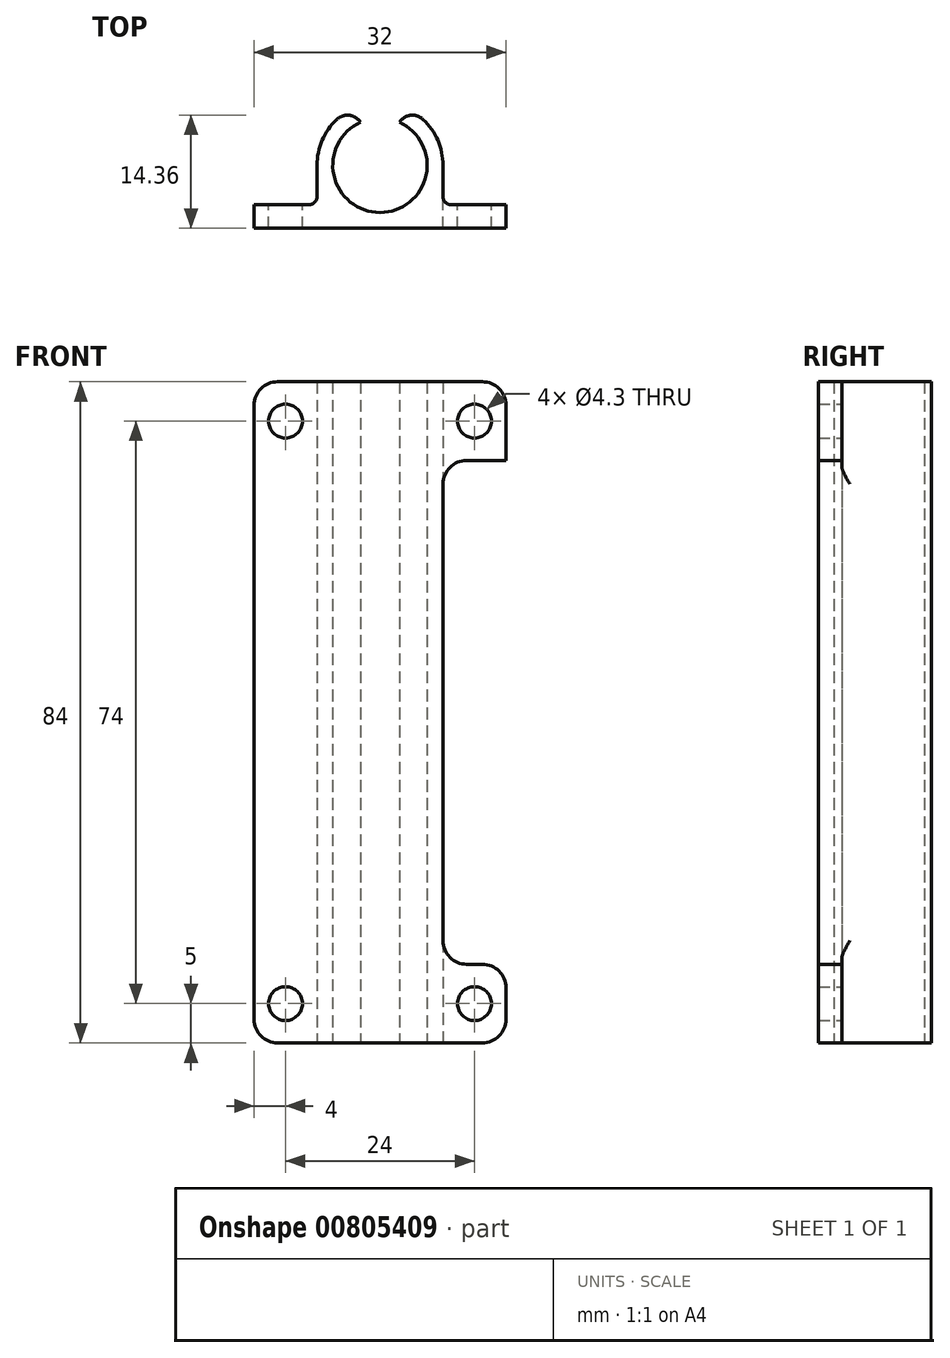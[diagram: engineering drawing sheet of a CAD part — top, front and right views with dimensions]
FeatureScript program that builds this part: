
annotation { "Feature Type Name" : "Feature", "Feature Type Description" : "" }
export const myFeature = defineFeature(function(context is Context, id is Id, definition is map)
    precondition{}
    {
        {
            var Q0;
            Q0=qCreatedBy(makeId("Top.planeOp"),FACE);
            var sketch = newSketch(context, id + "F0", { "sketchPlane" : qUnion([Q0])});
            skArc(sketch, "E0", {"start": v(-2.46, 5.47) * mm, "mid": v(0, -6) * mm, "end": v(2.46, 5.47) * mm});
            skArc(sketch, "E1", {"start": v(-2.5, 7.6) * mm, "mid": v(0, -8) * mm, "end": v(2.5, 7.6) * mm});
            skLineSegment(sketch, "E2", {"start": v(-8, 0) * mm, "end": v(-8, -8) * mm});
            skLineSegment(sketch, "E3", {"start": v(8, 0) * mm, "end": v(8, -8) * mm});
            skLineSegment(sketch, "E4", {"start": v(8, -8) * mm, "end": v(2.5, -8) * mm});
            skLineSegment(sketch, "E5.bottom", {"start": v(-8, -5) * mm, "end": v(-16, -5) * mm});
            skLineSegment(sketch, "E5.top", {"start": v(-8, -8) * mm, "end": v(-16, -8) * mm});
            skLineSegment(sketch, "E5.left", {"start": v(-8, -5) * mm, "end": v(-8, -8) * mm});
            skLineSegment(sketch, "E5.right", {"start": v(-16, -5) * mm, "end": v(-16, -8) * mm});
            skLineSegment(sketch, "E6.bottom", {"start": v(8, -8) * mm, "end": v(16, -8) * mm});
            skLineSegment(sketch, "E6.top", {"start": v(8, -5) * mm, "end": v(16, -5) * mm});
            skLineSegment(sketch, "E6.left", {"start": v(8, -8) * mm, "end": v(8, -5) * mm});
            skLineSegment(sketch, "E6.right", {"start": v(16, -8) * mm, "end": v(16, -5) * mm});
            skLineSegment(sketch, "E7", {"start": v(0, -8) * mm, "end": v(-2.5, -8) * mm});
            skLineSegment(sketch, "E8", {"start": v(0, -8) * mm, "end": v(2.5, -8) * mm});
            skLineSegment(sketch, "E9.trimOffspring", {"start": v(-2.46, 5.47) * mm, "end": v(-2.5, 7.6) * mm});
            skLineSegment(sketch, "E10.trimOffspring", {"start": v(2.46, 5.47) * mm, "end": v(2.5, 7.6) * mm});
            skLineSegment(sketch, "E11.trimOffspring", {"start": v(-2.5, -8) * mm, "end": v(-8, -8) * mm});
            skSolve(sketch);
        }
        {
            var Q0;
            Q0=makeQuery(id+"F0.imprint","IMPRINT",FACE,{"disambiguationData":[TD([[makeQuery(id+"F0.imprint","IMPRINT",EDGE,{"derivedFrom":sQuery(id+"F0.wireOp",EDGE,"E5.bottom")}),1.0]])]});
            var Q1;
            {var subQ1=sQuery(id+"F0.wireOp",EDGE,"E2");Q1=makeQuery(id+"F0.imprint","IMPRINT",FACE,{"disambiguationData":[TD([[makeQuery(id+"F0.imprint","IMPRINT",EDGE,{"derivedFrom":subQ1}),1.0]])]});}
            var Q2;
            Q2=makeQuery(id+"F0.imprint","IMPRINT",FACE,{"disambiguationData":[TD([[makeQuery(id+"F0.imprint","IMPRINT",EDGE,{"derivedFrom":sQuery(id+"F0.wireOp",EDGE,"E0")}),-1.0]])]});
            var Q3;
            {var subQ0=sQuery(id+"F0.wireOp",EDGE,"E3");Q3=makeQuery(id+"F0.imprint","IMPRINT",FACE,{"disambiguationData":[TD([[makeQuery(id+"F0.imprint","IMPRINT",EDGE,{"derivedFrom":subQ0}),-1.0]])]});}
            var Q4;
            Q4=makeQuery(id+"F0.imprint","IMPRINT",FACE,{"disambiguationData":[TD([[makeQuery(id+"F0.imprint","IMPRINT",EDGE,{"derivedFrom":sQuery(id+"F0.wireOp",EDGE,"E6.bottom")}),1.0]])]});
            extrude(context, id + "F1", {"entities" : qUnion([Q0, Q1, Q2, Q3, Q4]), "depth" : 84 * mm, "offsetDistance" : 25 * mm});
        }
        {
            var Q0;
            Q0=qCreatedBy(makeId("Front.planeOp"),FACE);
            var sketch = newSketch(context, id + "F2", { "sketchPlane" : qUnion([Q0])});
            skPoint(sketch, "E12", {"position": v(12, 79) * mm});
            skPoint(sketch, "E13", {"position": v(-12, 79) * mm});
            skPoint(sketch, "E14", {"position": v(12, 5) * mm});
            skPoint(sketch, "E15", {"position": v(-12, 5) * mm});
            skLineSegment(sketch, "E16", {"start": v(0, 10) * mm, "end": v(16, 10) * mm});
            skLineSegment(sketch, "E17", {"start": v(0, 74) * mm, "end": v(16, 74) * mm});
            skLineSegment(sketch, "E18", {"start": v(8, 74) * mm, "end": v(8, 10) * mm});
            skLineSegment(sketch, "E19", {"start": v(0, 74) * mm, "end": v(-16, 74) * mm});
            skLineSegment(sketch, "E20", {"start": v(0, 10) * mm, "end": v(-16, 10) * mm});
            skLineSegment(sketch, "E21", {"start": v(-8, 10) * mm, "end": v(-8, 74) * mm});
            skLineSegment(sketch, "E22", {"start": v(16, 74) * mm, "end": v(16, 10) * mm});
            skLineSegment(sketch, "E23.MirrorCS", {"start": v(-8, 74) * mm, "end": v(-8, 10) * mm});
            skLineSegment(sketch, "E24.MirrorCS", {"start": v(-16, 74) * mm, "end": v(-16, 10) * mm});
            skSolve(sketch);
        }
        {
            var Q0;
            Q0=sQuery(id+"F2.wireOp",VERTEX,"E14");
            var Q1;
            Q1=sQuery(id+"F2.wireOp",VERTEX,"E15");
            var Q2;
            Q2=sQuery(id+"F2.wireOp",VERTEX,"E12");
            var Q3;
            Q3=sQuery(id+"F2.wireOp",VERTEX,"E13");
            var Q4;
            Q4=makeQuery(id+"F1.opExtrude","SWEPT_BODY",BODY,{"disambiguationData":[OSD([sQuery(id+"F0.wireOp",EDGE,"E0"),sQuery(id+"F0.wireOp",EDGE,"E1"),sQuery(id+"F0.wireOp",EDGE,"E2"),sQuery(id+"F0.wireOp",EDGE,"E3"),sQuery(id+"F0.wireOp",EDGE,"E4"),sQuery(id+"F0.wireOp",EDGE,"E5.bottom"),sQuery(id+"F0.wireOp",EDGE,"E5.top"),sQuery(id+"F0.wireOp",EDGE,"E5.right"),sQuery(id+"F0.wireOp",EDGE,"E6.bottom"),sQuery(id+"F0.wireOp",EDGE,"E6.top"),sQuery(id+"F0.wireOp",EDGE,"E6.right"),sQuery(id+"F0.wireOp",EDGE,"E7"),sQuery(id+"F0.wireOp",EDGE,"E8"),sQuery(id+"F0.wireOp",EDGE,"E9.trimOffspring"),sQuery(id+"F0.wireOp",EDGE,"E10.trimOffspring"),sQuery(id+"F0.wireOp",EDGE,"E11.trimOffspring")])]});
            hole(context, id + "F3", {"style" : HoleStyle.SIMPLE, "endStyle" : HoleEndStyle.BLIND, "oppositeDirection" : true, "holeDiameter" : 4.3 * mm, "majorDiameter" : 5 * mm, "holeDepth" : 16 * mm, "isTappedThrough" : true, "tappedDepth" : 12 * mm, "tapClearance" : 3, "locations" : qUnion([Q0, Q1, Q2, Q3]), "scope" : qUnion([Q4])});
        }
        {
            var Q0;
            {var subQ0=sQuery(id+"F2.wireOp",EDGE,"E22");Q0=makeQuery(id+"F2.imprint","IMPRINT",FACE,{"disambiguationData":[TD([[makeQuery(id+"F2.imprint","IMPRINT",EDGE,{"derivedFrom":subQ0}),-1.0]])]});}
            var Q1;
            {var subQ2=sQuery(id+"F2.wireOp",EDGE,"E23.MirrorCS");Q1=makeQuery(id+"F2.imprint","IMPRINT",FACE,{"disambiguationData":[TD([[makeQuery(id+"F2.imprint","IMPRINT",EDGE,{"derivedFrom":subQ2}),-1.0]])]});}
            extrude(context, id + "F4", {"entities" : qUnion([Q0, Q1]), "operationType" : NewBodyOperationType.REMOVE, "depth" : 25 * mm, "offsetDistance" : 25 * mm});
        }
        {
            var Q0;
            Q0=makeQuery(id+"F1.opExtrude","CAP_EDGE",EDGE,{"disambiguationData":[OSD([sQuery(id+"F0.wireOp",EDGE,"E5.right")])],"isStart":false});
            var Q1;
            Q1=makeQuery(id+"F4.boolean.opBoolean","COPY",EDGE,{"derivedFrom":makeQuery(id+"F4.opExtrude","SWEPT_EDGE",EDGE,{"disambiguationData":[OSD([sQuery(id+"F2.wireOp",EDGE,"E19"),sQuery(id+"F2.wireOp",EDGE,"E24.MirrorCS")])]})});
            var Q2;
            Q2=makeQuery(id+"F1.opExtrude","CAP_EDGE",EDGE,{"disambiguationData":[OSD([sQuery(id+"F0.wireOp",EDGE,"E6.right")])],"isStart":false});
            var Q3;
            Q3=makeQuery(id+"F4.boolean.opBoolean","COPY",EDGE,{"derivedFrom":makeQuery(id+"F4.opExtrude","SWEPT_EDGE",EDGE,{"disambiguationData":[OSD([sQuery(id+"F2.wireOp",EDGE,"E17"),sQuery(id+"F2.wireOp",EDGE,"E22")])]})});
            var Q4;
            Q4=makeQuery(id+"F1.opExtrude","CAP_EDGE",EDGE,{"disambiguationData":[OSD([sQuery(id+"F0.wireOp",EDGE,"E5.right")])],"isStart":true});
            var Q5;
            Q5=makeQuery(id+"F1.opExtrude","CAP_EDGE",EDGE,{"disambiguationData":[OSD([sQuery(id+"F0.wireOp",EDGE,"E6.right")])],"isStart":true});
            var Q6;
            Q6=makeQuery(id+"F4.boolean.opBoolean","COPY",EDGE,{"derivedFrom":makeQuery(id+"F4.opExtrude","SWEPT_EDGE",EDGE,{"disambiguationData":[OSD([sQuery(id+"F2.wireOp",EDGE,"E16"),sQuery(id+"F2.wireOp",EDGE,"E22")])]})});
            var Q7;
            Q7=makeQuery(id+"F4.boolean.opBoolean","COPY",EDGE,{"derivedFrom":makeQuery(id+"F4.opExtrude","SWEPT_EDGE",EDGE,{"disambiguationData":[OSD([sQuery(id+"F2.wireOp",EDGE,"E20"),sQuery(id+"F2.wireOp",EDGE,"E24.MirrorCS")])]})});
            var Q8;
            Q8=makeQuery(id+"F4.boolean.opBoolean","COPY",EDGE,{"derivedFrom":makeQuery(id+"F4.opExtrude","SWEPT_EDGE",EDGE,{"disambiguationData":[OSD([sQuery(id+"F2.wireOp",EDGE,"E20"),sQuery(id+"F2.wireOp",EDGE,"E23.MirrorCS")])]})});
            var Q9;
            Q9=makeQuery(id+"F4.boolean.opBoolean","COPY",EDGE,{"derivedFrom":makeQuery(id+"F4.opExtrude","SWEPT_EDGE",EDGE,{"disambiguationData":[OSD([sQuery(id+"F2.wireOp",EDGE,"E16"),sQuery(id+"F2.wireOp",EDGE,"E18")])]})});
            var Q10;
            Q10=makeQuery(id+"F4.boolean.opBoolean","COPY",EDGE,{"derivedFrom":makeQuery(id+"F4.opExtrude","SWEPT_EDGE",EDGE,{"disambiguationData":[OSD([sQuery(id+"F2.wireOp",EDGE,"E19"),sQuery(id+"F2.wireOp",EDGE,"E23.MirrorCS")])]})});
            var Q11;
            Q11=makeQuery(id+"F4.boolean.opBoolean","COPY",EDGE,{"derivedFrom":makeQuery(id+"F4.opExtrude","SWEPT_EDGE",EDGE,{"disambiguationData":[OSD([sQuery(id+"F2.wireOp",EDGE,"E17"),sQuery(id+"F2.wireOp",EDGE,"E18")])]})});
            fillet(context, id + "F5", {"entities" : qUnion([Q0, Q1, Q2, Q3, Q4, Q5, Q6, Q7, Q8, Q9, Q10, Q11]), "radius" : 3 * mm, "tangentPropagation" : true, "allowEdgeOverflow" : false});
        }
        {
            var Q0;
            {var subQ0=sQuery(id+"F0.wireOp",EDGE,"E5.bottom");var subQ1=sQuery(id+"F0.wireOp",EDGE,"E2");Q0=makeQuery(id+"F4.boolean.opBoolean","SPLIT",EDGE,{"disambiguationData":[TD([makeQuery(id+"F4.opExtrude","SWEPT_FACE",FACE,{"disambiguationData":[OSD([sQuery(id+"F2.wireOp",EDGE,"E20")])]})])],"derivedFrom":makeQuery(id+"F1.opExtrude","SWEPT_EDGE",EDGE,{"disambiguationData":[OSD([subQ1,subQ0,sQuery(id+"F0.wireOp",EDGE,"E5.left")])]})});}
            var Q1;
            {var subQ0=sQuery(id+"F0.wireOp",EDGE,"E6.top");var subQ1=sQuery(id+"F0.wireOp",EDGE,"E3");Q1=makeQuery(id+"F4.boolean.opBoolean","SPLIT",EDGE,{"disambiguationData":[TD([makeQuery(id+"F4.opExtrude","SWEPT_FACE",FACE,{"disambiguationData":[OSD([sQuery(id+"F2.wireOp",EDGE,"E16")])]})])],"derivedFrom":makeQuery(id+"F1.opExtrude","SWEPT_EDGE",EDGE,{"disambiguationData":[OSD([subQ1,subQ0,sQuery(id+"F0.wireOp",EDGE,"E6.left")])]})});}
            var Q2;
            {var subQ0=sQuery(id+"F0.wireOp",EDGE,"E6.top");var subQ1=sQuery(id+"F0.wireOp",EDGE,"E3");Q2=makeQuery(id+"F4.boolean.opBoolean","SPLIT",EDGE,{"disambiguationData":[TD([makeQuery(id+"F4.opExtrude","SWEPT_FACE",FACE,{"disambiguationData":[OSD([sQuery(id+"F2.wireOp",EDGE,"E17")])]})])],"derivedFrom":makeQuery(id+"F1.opExtrude","SWEPT_EDGE",EDGE,{"disambiguationData":[OSD([subQ1,subQ0,sQuery(id+"F0.wireOp",EDGE,"E6.left")])]})});}
            var Q3;
            {var subQ0=sQuery(id+"F0.wireOp",EDGE,"E5.bottom");var subQ1=sQuery(id+"F0.wireOp",EDGE,"E2");Q3=makeQuery(id+"F4.boolean.opBoolean","SPLIT",EDGE,{"disambiguationData":[TD([makeQuery(id+"F4.opExtrude","SWEPT_FACE",FACE,{"disambiguationData":[OSD([sQuery(id+"F2.wireOp",EDGE,"E19")])]})])],"derivedFrom":makeQuery(id+"F1.opExtrude","SWEPT_EDGE",EDGE,{"disambiguationData":[OSD([subQ1,subQ0,sQuery(id+"F0.wireOp",EDGE,"E5.left")])]})});}
            fillet(context, id + "F6", {"entities" : qUnion([Q0, Q1, Q2, Q3]), "radius" : 1 * mm, "tangentPropagation" : true, "allowEdgeOverflow" : false});
        }
        {
            var Q0;
            Q0=makeQuery(id+"F1.opExtrude","SWEPT_EDGE",EDGE,{"disambiguationData":[OSD([sQuery(id+"F0.wireOp",EDGE,"E1"),sQuery(id+"F0.wireOp",EDGE,"E10.trimOffspring")])]});
            var Q1;
            Q1=makeQuery(id+"F1.opExtrude","SWEPT_EDGE",EDGE,{"disambiguationData":[OSD([sQuery(id+"F0.wireOp",EDGE,"E1"),sQuery(id+"F0.wireOp",EDGE,"E9.trimOffspring")])]});
            fillet(context, id + "F7", {"entities" : qUnion([Q0, Q1]), "radius" : 2 * mm, "tangentPropagation" : true, "allowEdgeOverflow" : false});
        }
    });
